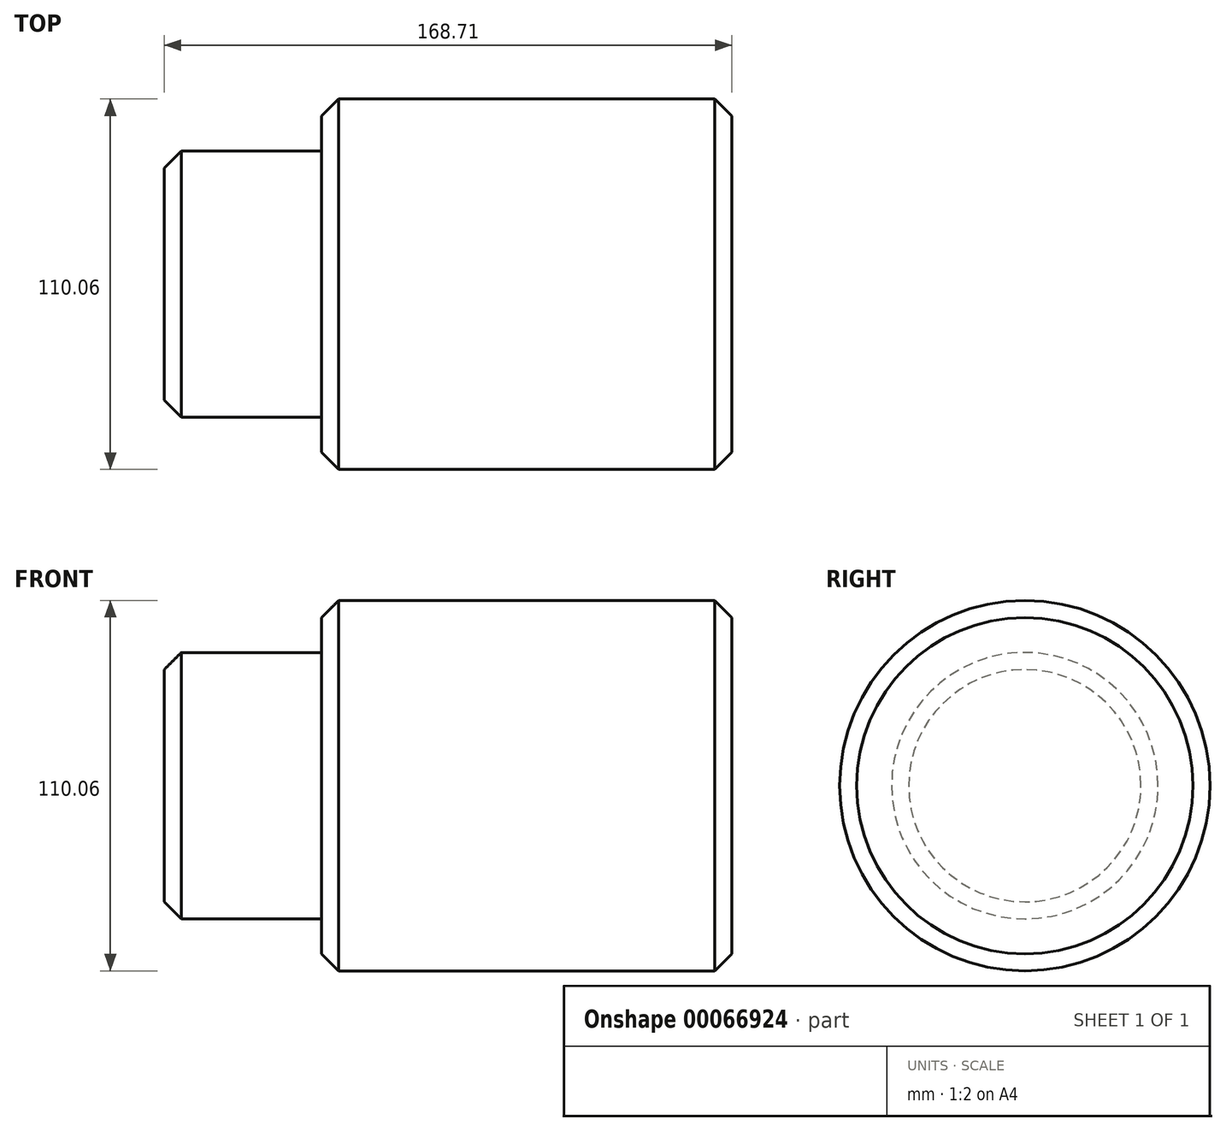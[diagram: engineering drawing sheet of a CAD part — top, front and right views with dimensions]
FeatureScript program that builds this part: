
annotation { "Feature Type Name" : "Feature", "Feature Type Description" : "" }
export const myFeature = defineFeature(function(context is Context, id is Id, definition is map)
    precondition{}
    {
        {
            var Q0;
            Q0=qCreatedBy(makeId("Front.planeOp"),FACE);
            var sketch = newSketch(context, id + "F0", { "sketchPlane" : qUnion([Q0])});
            skLineSegment(sketch, "E0", {"start": v(-46.73, 0) * mm, "end": v(-46.73, 39.6) * mm});
            skLineSegment(sketch, "E1", {"start": v(-46.73, 39.6) * mm, "end": v(0, 39.6) * mm});
            skLineSegment(sketch, "E2", {"start": v(0, 39.6) * mm, "end": v(0, 55.03) * mm});
            skLineSegment(sketch, "E3", {"start": v(0, 55.03) * mm, "end": v(121.98, 55.03) * mm});
            skLineSegment(sketch, "E4", {"start": v(121.98, 55.03) * mm, "end": v(121.98, 0) * mm});
            skLineSegment(sketch, "E5", {"start": v(-46.73, 0) * mm, "end": v(121.98, 0) * mm});
            skPoint(sketch, "E6.orphan", {"position": v(-49.99, 0) * mm});
            skSolve(sketch);
        }
        {
            var Q0;
            Q0=makeQuery(id+"F0.imprint","IMPRINT",FACE,{"disambiguationData":[TD([[makeQuery(id+"F0.imprint","IMPRINT",EDGE,{"derivedFrom":sQuery(id+"F0.wireOp",EDGE,"E0")}),-1.0]])]});
            var Q1;
            Q1=sQuery(id+"F0.wireOp",EDGE,"E5");
            revolve(context, id + "F1", {"entities" : qUnion([Q0]), "axis" : qUnion([Q1]), "revolveType" : RevolveType.FULL});
        }
        {
            var Q0;
            Q0=makeQuery(id+"F1.opRevolve","SWEPT_EDGE",EDGE,{"disambiguationData":[OSD([sQuery(id+"F0.wireOp",EDGE,"E0"),sQuery(id+"F0.wireOp",EDGE,"E1")])]});
            var Q1;
            Q1=makeQuery(id+"F1.opRevolve","SWEPT_EDGE",EDGE,{"disambiguationData":[OSD([sQuery(id+"F0.wireOp",EDGE,"E2"),sQuery(id+"F0.wireOp",EDGE,"E3")])]});
            var Q2;
            Q2=makeQuery(id+"F1.opRevolve","SWEPT_EDGE",EDGE,{"disambiguationData":[OSD([sQuery(id+"F0.wireOp",EDGE,"E3"),sQuery(id+"F0.wireOp",EDGE,"E4")])]});
            chamfer(context, id + "F2", {"entities" : qUnion([Q0, Q1, Q2]), "width" : 5.08 * mm, "tangentPropagation" : true});
        }
    });
